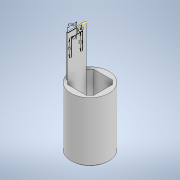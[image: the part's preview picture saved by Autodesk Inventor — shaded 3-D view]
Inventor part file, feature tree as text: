
AUTODESK INVENTOR PART (.ipt)
format: ipt  version: 2021 (Build 250183000, 183)  size: 147,456 bytes
history: native  units: mm
features: sketch x4, extrude x3, other x1
ambient origin geometry x8: Origin, YZ Plane, XZ Plane, XY Plane, X Axis, Y Axis, Z Axis, Center Point
bodies: Body1 (feature_tree)
feature tree (8):
  other  "Sólido1"
  extrude  "Extrusión1"  Depth=40.0mm TaperAngle=360.0deg
  extrude  "Extrusión2"  Depth=100.0mm
  extrude  "Extrusión4"  Depth=2.0mm TaperAngle=0.0deg
  sketch  "Boceto7"  dims[d38=2.0mm d39=70.0mm d40=0.0mm d41=16.0mm d42=10.0mm d43=9.5mm d44=9.5mm d45=29.0mm d46=29.0mm]
  sketch  "Boceto1"  dims[d3=22.5mm d5=40.0mm d7=360.0deg]
  sketch  "Boceto2"  dims[d9=100.0mm d10=0.0mm d11=59.6mm]
  sketch  "Boceto6"  dims[d12=60.5mm d13=2.0mm d14=0.0mm]
